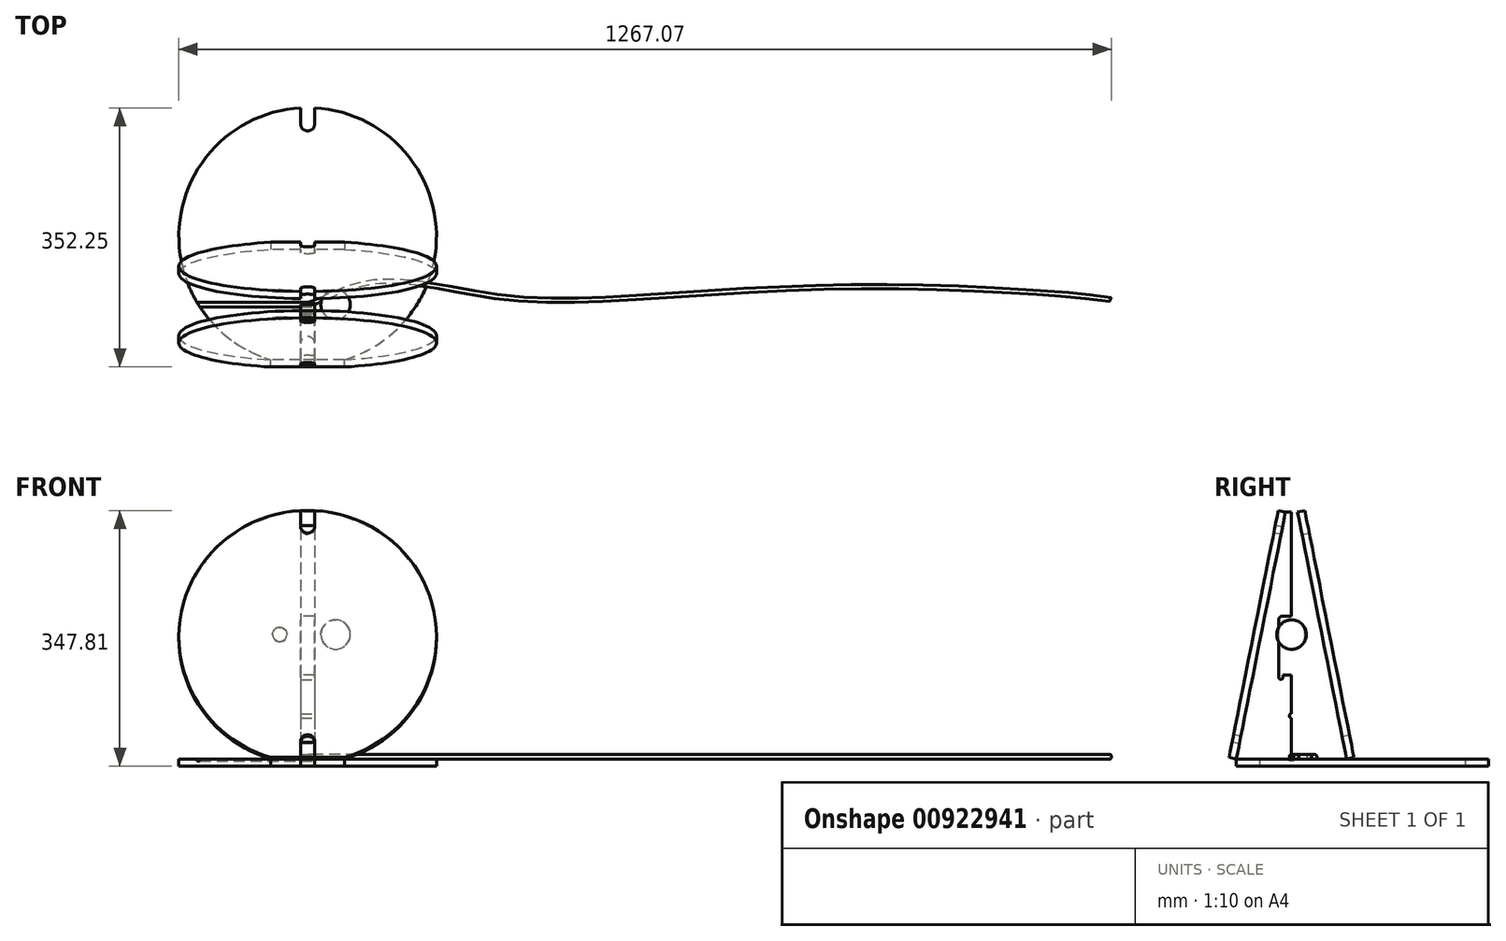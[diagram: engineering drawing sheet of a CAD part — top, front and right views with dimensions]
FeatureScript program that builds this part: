
annotation { "Feature Type Name" : "Feature", "Feature Type Description" : "" }
export const myFeature = defineFeature(function(context is Context, id is Id, definition is map)
    precondition{}
    {
        {
            var Q0;
            Q0=qCreatedBy(makeId("Front.planeOp"),FACE);
            var Q1;
            Q1=qCreatedBy(makeId("Top.planeOp"),FACE);
            cPlane(context, id + "F0", {"entities" : qUnion([Q0, Q1]), "cplaneType" : CPlaneType.MID_PLANE, "offset" : 25.4 * mm, "flipAlignment" : true, "width" : 152.4 * mm, "height" : 152.4 * mm});
        }
        {
            var Q0;
            Q0=qCreatedBy(id+"F0.planeOp",FACE);
            var Q1;
            Q1=qCreatedBy(makeId("Front.planeOp"),FACE);
            cPlane(context, id + "F1", {"entities" : qUnion([Q0, Q1]), "cplaneType" : CPlaneType.MID_PLANE, "offset" : 25.4 * mm, "flipAlignment" : true, "width" : 152.4 * mm, "height" : 152.4 * mm});
        }
        {
            var Q0;
            Q0=qCreatedBy(id+"F1.planeOp",FACE);
            var Q1;
            Q1=qCreatedBy(makeId("Front.planeOp"),FACE);
            cPlane(context, id + "F2", {"entities" : qUnion([Q0, Q1]), "cplaneType" : CPlaneType.MID_PLANE, "offset" : 25.4 * mm, "flipAlignment" : true, "width" : 152.4 * mm, "height" : 152.4 * mm});
        }
        {
            var Q0;
            Q0=qCreatedBy(id+"F2.planeOp",FACE);
            var sketch = newSketch(context, id + "F3", { "sketchPlane" : qUnion([Q0])});
            skArc(sketch, "E0", {"start": v(50, 0) * mm, "mid": v(0, 342.7) * mm, "end": v(-50, 0) * mm});
            skLineSegment(sketch, "E1", {"start": v(50, 0) * mm, "end": v(-50, 0) * mm});
            skSolve(sketch);
        }
        {
            var Q0;
            Q0=qSketchRegion(id+"F3",true);
            extrude(context, id + "F4", {"entities" : qUnion([Q0]), "depth" : 10 * mm, "offsetDistance" : 25 * mm});
        }
        {
            var Q0;
            Q0=qCreatedBy(makeId("Front.planeOp"),FACE);
            cPlane(context, id + "F5", {"entities" : qUnion([Q0]), "cplaneType" : CPlaneType.OFFSET, "offset" : 75 * mm, "oppositeDirection" : true, "width" : 150 * mm, "height" : 150 * mm});
        }
        {
            var Q0;
            Q0=makeQuery(id+"F4.opExtrude","CAP_FACE",FACE,{"disambiguationData":[OSD([sQuery(id+"F3.wireOp",EDGE,"E0"),sQuery(id+"F3.wireOp",EDGE,"E1")])],"isStart":false});
            var sketch = newSketch(context, id + "F6", { "sketchPlane" : qUnion([Q0])});
            skLineSegment(sketch, "E2.bottom", {"start": v(-9.6, -22) * mm, "end": v(9.6, -22) * mm});
            skLineSegment(sketch, "E2.left", {"start": v(-9.6, -22) * mm, "end": v(-9.6, 22) * mm});
            skLineSegment(sketch, "E2.right", {"start": v(9.6, -22) * mm, "end": v(9.6, 22) * mm});
            skPoint(sketch, "E2.middle", {"position": v(0, 0) * mm});
            skLineSegment(sketch, "E3.top", {"start": v(-9.6, 364.7) * mm, "end": v(9.6, 364.7) * mm});
            skLineSegment(sketch, "E3.left", {"start": v(-9.6, 320.7) * mm, "end": v(-9.6, 364.7) * mm});
            skLineSegment(sketch, "E3.right", {"start": v(9.6, 320.7) * mm, "end": v(9.6, 364.7) * mm});
            skPoint(sketch, "E3.middle", {"position": v(0, 342.7) * mm});
            skArc(sketch, "E4", {"start": v(9.6, 22) * mm, "mid": v(0, 31.6) * mm, "end": v(-9.6, 22) * mm});
            skArc(sketch, "E5", {"start": v(-9.6, 320.7) * mm, "mid": v(0, 311.1) * mm, "end": v(9.6, 320.7) * mm});
            skSolve(sketch);
        }
        {
            var Q0;
            Q0=qSketchRegion(id+"F6",true);
            extrude(context, id + "F7", {"entities" : qUnion([Q0]), "operationType" : NewBodyOperationType.REMOVE, "endBound" : BoundingType.THROUGH_ALL, "oppositeDirection" : true, "depth" : 25 * mm, "offsetDistance" : 25 * mm});
        }
        {
            var Q0;
            Q0=makeQuery(id+"F4.opExtrude","CAP_FACE",FACE,{"disambiguationData":[OSD([sQuery(id+"F3.wireOp",EDGE,"E0"),sQuery(id+"F3.wireOp",EDGE,"E1")])],"isStart":false});
            var sketch = newSketch(context, id + "F8", { "sketchPlane" : qUnion([Q0])});
            skArc(sketch, "E6.0", {"start": v(50, 0) * mm, "mid": v(173.8, 188.2) * mm, "end": v(9.6, 342.44) * mm});
            skLineSegment(sketch, "E6.1", {"start": v(50, 0) * mm, "end": v(9.6, 0) * mm});
            skLineSegment(sketch, "E7.1", {"start": v(-9.6, 0) * mm, "end": v(-9.6, 22) * mm});
            skLineSegment(sketch, "E7.2", {"start": v(9.6, 0) * mm, "end": v(9.6, 22) * mm});
            skPoint(sketch, "E7.3", {"position": v(0, 0) * mm});
            skLineSegment(sketch, "E7.5", {"start": v(-9.6, 320.7) * mm, "end": v(-9.6, 342.44) * mm});
            skLineSegment(sketch, "E7.6", {"start": v(9.6, 320.7) * mm, "end": v(9.6, 342.44) * mm});
            skPoint(sketch, "E7.7", {"position": v(0, 342.7) * mm});
            skArc(sketch, "E7.8", {"start": v(9.6, 22) * mm, "mid": v(0, 31.6) * mm, "end": v(-9.6, 22) * mm});
            skArc(sketch, "E7.9", {"start": v(-9.6, 320.7) * mm, "mid": v(0, 311.1) * mm, "end": v(9.6, 320.7) * mm});
            skPoint(sketch, "E7.4.end.orphan", {"position": v(9.6, 364.7) * mm});
            skPoint(sketch, "E7.4.start.orphan", {"position": v(-9.6, 364.7) * mm});
            skArc(sketch, "E8.trimOffspring", {"start": v(-9.6, 342.44) * mm, "mid": v(-173.8, 188.2) * mm, "end": v(-50, 0) * mm});
            skPoint(sketch, "E7.0.end.orphan", {"position": v(9.6, -22) * mm});
            skPoint(sketch, "E7.0.start.orphan", {"position": v(-9.6, -22) * mm});
            skLineSegment(sketch, "E9.trimOffspring", {"start": v(-9.6, 0) * mm, "end": v(-50, 0) * mm});
            skSolve(sketch);
        }
        {
            var Q0;
            Q0=makeQuery(id+"F4.opExtrude","SWEPT_BODY",BODY,{"disambiguationData":[OSD([sQuery(id+"F3.wireOp",EDGE,"E0"),sQuery(id+"F3.wireOp",EDGE,"E1")])]});
            var Q1;
            Q1=makeQuery(id+"F1jAScYJ9BiHF60_4.opExtrude","SWEPT_BODY",BODY,{"disambiguationData":[OSD([sQuery(id+"F8.wireOp",EDGE,"E6.0"),sQuery(id+"F8.wireOp",EDGE,"E6.1"),sQuery(id+"F8.wireOp",EDGE,"E7.1"),sQuery(id+"F8.wireOp",EDGE,"E7.2"),sQuery(id+"F8.wireOp",EDGE,"E7.5"),sQuery(id+"F8.wireOp",EDGE,"E7.6"),sQuery(id+"F8.wireOp",EDGE,"E7.8"),sQuery(id+"F8.wireOp",EDGE,"E7.9"),sQuery(id+"F8.wireOp",EDGE,"E8.trimOffspring"),sQuery(id+"F8.wireOp",EDGE,"E9.trimOffspring")])]});
            var Q2;
            Q2=makeQuery(id+"FZ6tUxqLbVE1ZoO_5.opPattern","COPY",BODY,{"derivedFrom":makeQuery(id+"F1jAScYJ9BiHF60_4.opExtrude","SWEPT_BODY",BODY,{"disambiguationData":[OSD([sQuery(id+"F8.wireOp",EDGE,"E6.0"),sQuery(id+"F8.wireOp",EDGE,"E6.1"),sQuery(id+"F8.wireOp",EDGE,"E7.1"),sQuery(id+"F8.wireOp",EDGE,"E7.2"),sQuery(id+"F8.wireOp",EDGE,"E7.5"),sQuery(id+"F8.wireOp",EDGE,"E7.6"),sQuery(id+"F8.wireOp",EDGE,"E7.8"),sQuery(id+"F8.wireOp",EDGE,"E7.9"),sQuery(id+"F8.wireOp",EDGE,"E8.trimOffspring"),sQuery(id+"F8.wireOp",EDGE,"E9.trimOffspring")])]}),"instanceName":"1"});
            var Q3;
            Q3=qCreatedBy(id+"F5.planeOp",FACE);
            mirror(context, id + "F9", {"entities" : qUnion([Q0, Q1, Q2]), "mirrorPlane" : qUnion([Q3])});
        }
        {
            var Q0;
            Q0=qCreatedBy(makeId("Right.planeOp"),FACE);
            var sketch = newSketch(context, id + "F10", { "sketchPlane" : qUnion([Q0])});
            skLineSegment(sketch, "E10", {"start": v(0, 0) * mm, "end": v(75, 0) * mm});
            skLineSegment(sketch, "E11", {"start": v(62.7, 315.25) * mm, "end": v(4.1, 20.6) * mm});
            skLineSegment(sketch, "E12", {"start": v(4.1, 20.6) * mm, "end": v(-5.71, 22.55) * mm});
            skLineSegment(sketch, "E13", {"start": v(-5.71, 22.55) * mm, "end": v(-9.8, 1.95) * mm});
            skLineSegment(sketch, "E14", {"start": v(-9.8, 1.95) * mm, "end": v(0, 0) * mm});
            skLineSegment(sketch, "E15", {"start": v(62.7, 315.25) * mm, "end": v(52.9, 317.2) * mm});
            skLineSegment(sketch, "E16", {"start": v(52.9, 317.2) * mm, "end": v(57, 337.8) * mm});
            skLineSegment(sketch, "E17", {"start": v(57, 337.8) * mm, "end": v(75, 337.8) * mm, "construction": true});
            skLineSegment(sketch, "E18", {"start": v(66.8, 335.85) * mm, "end": v(57, 337.8) * mm});
            skLineSegment(sketch, "E19", {"start": v(66.8, 335.85) * mm, "end": v(75, 335.85) * mm});
            skLineSegment(sketch, "E20", {"start": v(75, 335.85) * mm, "end": v(75, 0) * mm, "construction": true});
            skLineSegment(sketch, "E21", {"start": v(75, 335.85) * mm, "end": v(75, 0) * mm});
            skSolve(sketch);
        }
        {
            var Q0;
            Q0=qSketchRegion(id+"F10",true);
            extrude(context, id + "F11", {"entities" : qUnion([Q0]), "depth" : (19 / 2) * mm, "offsetDistance" : 25 * mm, "hasSecondDirection" : true, "secondDirectionOppositeDirection" : true, "secondDirectionDepth" : (19 / 2) * mm});
        }
        {
            var Q0;
            Q0=qCreatedBy(makeId("Top.planeOp"),FACE);
            cPlane(context, id + "F12", {"entities" : qUnion([Q0]), "cplaneType" : CPlaneType.OFFSET, "offset" : 3 * mm, "width" : 150 * mm, "height" : 150 * mm});
        }
        {
            var Q0;
            Q0=qCreatedBy(id+"F12.planeOp",FACE);
            var sketch = newSketch(context, id + "F13", { "sketchPlane" : qUnion([Q0])});
            skFitSpline(sketch, "E22", {"points": [v(0, 75) * mm, v(84.05, 104.6) * mm, v(247.75, 87.31) * mm, v(416.38, 82.9) * mm, v(763.05, 99.39) * mm, v(1090.84, 82.03) * mm], "startDerivative": vector(418.66, 113.12) * mm, "endDerivative": vector(571.08, -92.4) * mm});
            skSolve(sketch);
        }
        {
            var Q0;
            Q0=qCreatedBy(makeId("Right.planeOp"),FACE);
            var sketch = newSketch(context, id + "F14", { "sketchPlane" : qUnion([Q0])});
            skCircle(sketch, "E23", {"center": v(75, 3) * mm, "radius": 3 * mm});
            skSolve(sketch);
        }
        {
            var Q0;
            Q0=qSketchRegion(id+"F14",true);
            var Q1;
            Q1=qConstructionFilter(qBodyType(qCreatedBy(id+"F13",EDGE),BodyType.WIRE),ConstructionObject.NO);
            sweep(context, id + "F15", {"profiles" : qUnion([Q0]), "path" : qUnion([Q1])});
        }
        {
            var Q0;
            Q0=qCreatedBy(id+"F5.planeOp",FACE);
            var sketch = newSketch(context, id + "F16", { "sketchPlane" : qUnion([Q0])});
            skArc(sketch, "E24", {"start": v(37.93, 189.08) * mm, "mid": v(17.85, 169.08) * mm, "end": v(37.93, 149.08) * mm});
            skLineSegment(sketch, "E25", {"start": v(37.93, 189.08) * mm, "end": v(37.93, 149.08) * mm});
            skSolve(sketch);
        }
        {
            var Q0;
            Q0=qSketchRegion(id+"F16",true);
            var Q1;
            Q1=sQuery(id+"F16.wireOp",EDGE,"E24");
            var Q2;
            Q2=sQuery(id+"F16.wireOp",EDGE,"E25");
            var Q3;
            Q3=sQuery(id+"F16.wireOp",EDGE,"E25");
            revolve(context, id + "F17", {"surfaceOperationType" : NewSurfaceOperationType.NEW, "entities" : qUnion([Q0]), "surfaceEntities" : qUnion([Q1, Q2]), "axis" : qUnion([Q3]), "revolveType" : RevolveType.FULL});
        }
        {
            var Q0;
            Q0=makeQuery(id+"F17.opRevolve","SWEPT_BODY",BODY,{"disambiguationData":[OSD([sQuery(id+"F16.wireOp",EDGE,"E24"),sQuery(id+"F16.wireOp",EDGE,"E25")])]});
            var Q1;
            Q1=qCreatedBy(makeId("Right.planeOp"),FACE);
            mirror(context, id + "F18", {"entities" : qUnion([Q0]), "mirrorPlane" : qUnion([Q1])});
        }
        {
            var Q0;
            Q0=makeQuery(id+"F11.opExtrude","SWEPT_EDGE",EDGE,{"disambiguationData":[OSD([sQuery(id+"F10.wireOp",EDGE,"E11"),sQuery(id+"F10.wireOp",EDGE,"E15")])]});
            var Q1;
            Q1=makeQuery(id+"F11.opExtrude","SWEPT_EDGE",EDGE,{"disambiguationData":[OSD([sQuery(id+"F10.wireOp",EDGE,"E11"),sQuery(id+"F10.wireOp",EDGE,"E12")])]});
            var Q2;
            Q2=makeQuery(id+"F6nMErL9dG46YH1_2.opPattern","COPY",EDGE,{"derivedFrom":makeQuery(id+"F11.opExtrude","SWEPT_EDGE",EDGE,{"disambiguationData":[OSD([sQuery(id+"F10.wireOp",EDGE,"E11"),sQuery(id+"F10.wireOp",EDGE,"E12")])]}),"instanceName":"1"});
            var Q3;
            Q3=makeQuery(id+"F6nMErL9dG46YH1_2.opPattern","COPY",EDGE,{"derivedFrom":makeQuery(id+"F11.opExtrude","SWEPT_EDGE",EDGE,{"disambiguationData":[OSD([sQuery(id+"F10.wireOp",EDGE,"E11"),sQuery(id+"F10.wireOp",EDGE,"E15")])]}),"instanceName":"1"});
            var Q4;
            Q4=makeQuery(id+"F6nMErL9dG46YH1_2.1.F11.opExtrude","SWEPT_EDGE",EDGE,{"disambiguationData":[OSD([sQuery(id+"F10.wireOp",EDGE,"E11"),sQuery(id+"F10.wireOp",EDGE,"E12")])]});
            var Q5;
            Q5=makeQuery(id+"F6nMErL9dG46YH1_2.1.F11.opExtrude","SWEPT_EDGE",EDGE,{"disambiguationData":[OSD([sQuery(id+"F10.wireOp",EDGE,"E11"),sQuery(id+"F10.wireOp",EDGE,"E15")])]});
            fillet(context, id + "F19", {"entities" : qUnion([Q0, Q1, Q2, Q3, Q4, Q5]), "radius" : 3 * mm, "tangentPropagation" : true, "allowEdgeOverflow" : false});
        }
        {
            var Q0;
            {var subQ0=makeQuery(id+"F11.opExtrude","CAP_FACE",FACE,{"disambiguationData":[OSD([sQuery(id+"F10.wireOp",EDGE,"E10"),sQuery(id+"F10.wireOp",EDGE,"XCGjGZEb-5ekM-1y0Q-NnFh-Xt25lKIHjE2G"),sQuery(id+"F10.wireOp",EDGE,"E11"),sQuery(id+"F10.wireOp",EDGE,"E12"),sQuery(id+"F10.wireOp",EDGE,"E13"),sQuery(id+"F10.wireOp",EDGE,"E14"),sQuery(id+"F10.wireOp",EDGE,"E15"),sQuery(id+"F10.wireOp",EDGE,"E16"),sQuery(id+"F10.wireOp",EDGE,"E17")])],"isStart":false});Q0=makeQuery(id+"F6nMErL9dG46YH1_2.boolean.opBoolean","MERGE",FACE,{"derivedFrom":[subQ0,makeQuery(id+"F6nMErL9dG46YH1_2.opPattern","COPY",FACE,{"derivedFrom":subQ0,"instanceName":"1"})]});}
            var sketch = newSketch(context, id + "F20", { "sketchPlane" : qUnion([Q0])});
            skSolve(sketch);
        }
        {
            var Q0;
            Q0=qCreatedBy(id+"F2.planeOp",FACE);
            var Q1;
            Q1=qCreatedBy(makeId("Top.planeOp"),FACE);
            cPlane(context, id + "F21", {"entities" : qUnion([Q0, Q1]), "cplaneType" : CPlaneType.MID_PLANE, "offset" : 25 * mm, "flipAlignment" : true, "width" : 150 * mm, "height" : 150 * mm});
        }
        {
            var Q0;
            Q0=makeQuery(id+"F4.opExtrude","SWEPT_BODY",BODY,{"disambiguationData":[OSD([sQuery(id+"F3.wireOp",EDGE,"E0"),sQuery(id+"F3.wireOp",EDGE,"E1")])]});
            var Q1;
            Q1=qCreatedBy(id+"F21.planeOp",FACE);
            mirror(context, id + "F22", {"entities" : qUnion([Q0]), "mirrorPlane" : qUnion([Q1])});
        }
        {
            var Q0;
            {var subQ3=sQuery(id+"F10.wireOp",EDGE,"E13");Q0=makeQuery(id+"F20.imprint","IMPRINT",FACE,{"disambiguationData":[TD([[makeQuery(id+"F20.imprint","IMPRINT",EDGE,{"derivedFrom":makeQuery(id+"F11.opExtrude","CAP_EDGE",EDGE,{"disambiguationData":[OSD([subQ3])],"isStart":false})}),1.0]])]});}
            var sketch = newSketch(context, id + "F23", { "sketchPlane" : qUnion([Q0])});
            skLineSegment(sketch, "E26", {"start": v(75, 0) * mm, "end": v(75, 150) * mm, "construction": true});
            skArc(sketch, "E27", {"start": v(92.5, 114.03) * mm, "mid": v(75, 190) * mm, "end": v(57.5, 114.03) * mm, "construction": true});
            skLineSegment(sketch, "E28", {"start": v(63.6, 114.03) * mm, "end": v(92.5, 114.03) * mm});
            skLineSegment(sketch, "E29.bottom", {"start": v(78.05, -3) * mm, "end": v(71.95, -3) * mm});
            skLineSegment(sketch, "E29.top", {"start": v(78.05, 3) * mm, "end": v(71.95, 3) * mm, "construction": true});
            skLineSegment(sketch, "E29.left", {"start": v(78.05, -3) * mm, "end": v(78.05, 3) * mm});
            skLineSegment(sketch, "E29.right", {"start": v(71.95, -3) * mm, "end": v(71.95, 3) * mm});
            skPoint(sketch, "E29.middle", {"position": v(75, 0) * mm});
            skArc(sketch, "E30", {"start": v(78.05, 3) * mm, "mid": v(75, 6.05) * mm, "end": v(71.95, 3) * mm});
            skLineSegment(sketch, "E31", {"start": v(57.5, 114.03) * mm, "end": v(57.5, 194.03) * mm});
            skLineSegment(sketch, "E32", {"start": v(57.5, 194.03) * mm, "end": v(92.5, 194.03) * mm});
            skLineSegment(sketch, "E33", {"start": v(92.5, 194.03) * mm, "end": v(92.5, 114.03) * mm});
            skLineSegment(sketch, "E34", {"start": v(75, 114.03) * mm, "end": v(75, 3) * mm, "construction": true});
            skCircle(sketch, "E35", {"center": v(75, 58.52) * mm, "radius": 3.05 * mm});
            skLineSegment(sketch, "E36.top", {"start": v(57.5, 111.03) * mm, "end": v(63.6, 111.03) * mm, "construction": true});
            skLineSegment(sketch, "E36.left", {"start": v(57.5, 114.03) * mm, "end": v(57.5, 111.03) * mm});
            skLineSegment(sketch, "E36.right", {"start": v(63.6, 114.03) * mm, "end": v(63.6, 111.03) * mm});
            skArc(sketch, "E37.trimOffspring", {"start": v(57.5, 111.03) * mm, "mid": v(60.55, 107.98) * mm, "end": v(63.6, 111.03) * mm});
            skSolve(sketch);
        }
        {
            var Q0;
            Q0 = qSketchRegion(id + "F23", true);
            extrude(context, id + "F24", {"entities" : qUnion([Q0]), "operationType" : NewBodyOperationType.REMOVE, "endBound" : BoundingType.THROUGH_ALL, "oppositeDirection" : true, "depth" : 25 * mm, "offsetDistance" : 25 * mm});
        }
        {
            var Q0;
            Q0=makeQuery(id+"F24.boolean.opBoolean","COPY",EDGE,{"derivedFrom":makeQuery(id+"F24.opExtrude","SWEPT_EDGE",EDGE,{"disambiguationData":[OSD([sQuery(id+"F23.wireOp",EDGE,"E28"),sQuery(id+"F23.wireOp",EDGE,"E33")])]})});
            var Q1;
            Q1=makeQuery(id+"F24.boolean.opBoolean","COPY",EDGE,{"derivedFrom":makeQuery(id+"F24.opExtrude","SWEPT_EDGE",EDGE,{"disambiguationData":[OSD([sQuery(id+"F23.wireOp",EDGE,"E31"),sQuery(id+"F23.wireOp",EDGE,"E32")])]})});
            var Q2;
            Q2=makeQuery(id+"F24.boolean.opBoolean","COPY",EDGE,{"derivedFrom":makeQuery(id+"F24.opExtrude","SWEPT_EDGE",EDGE,{"disambiguationData":[OSD([sQuery(id+"F23.wireOp",EDGE,"E32"),sQuery(id+"F23.wireOp",EDGE,"E33")])]})});
            fillet(context, id + "F25", {"entities" : qUnion([Q0, Q1, Q2]), "radius" : 5 * mm, "tangentPropagation" : true, "allowEdgeOverflow" : false});
        }
    });
